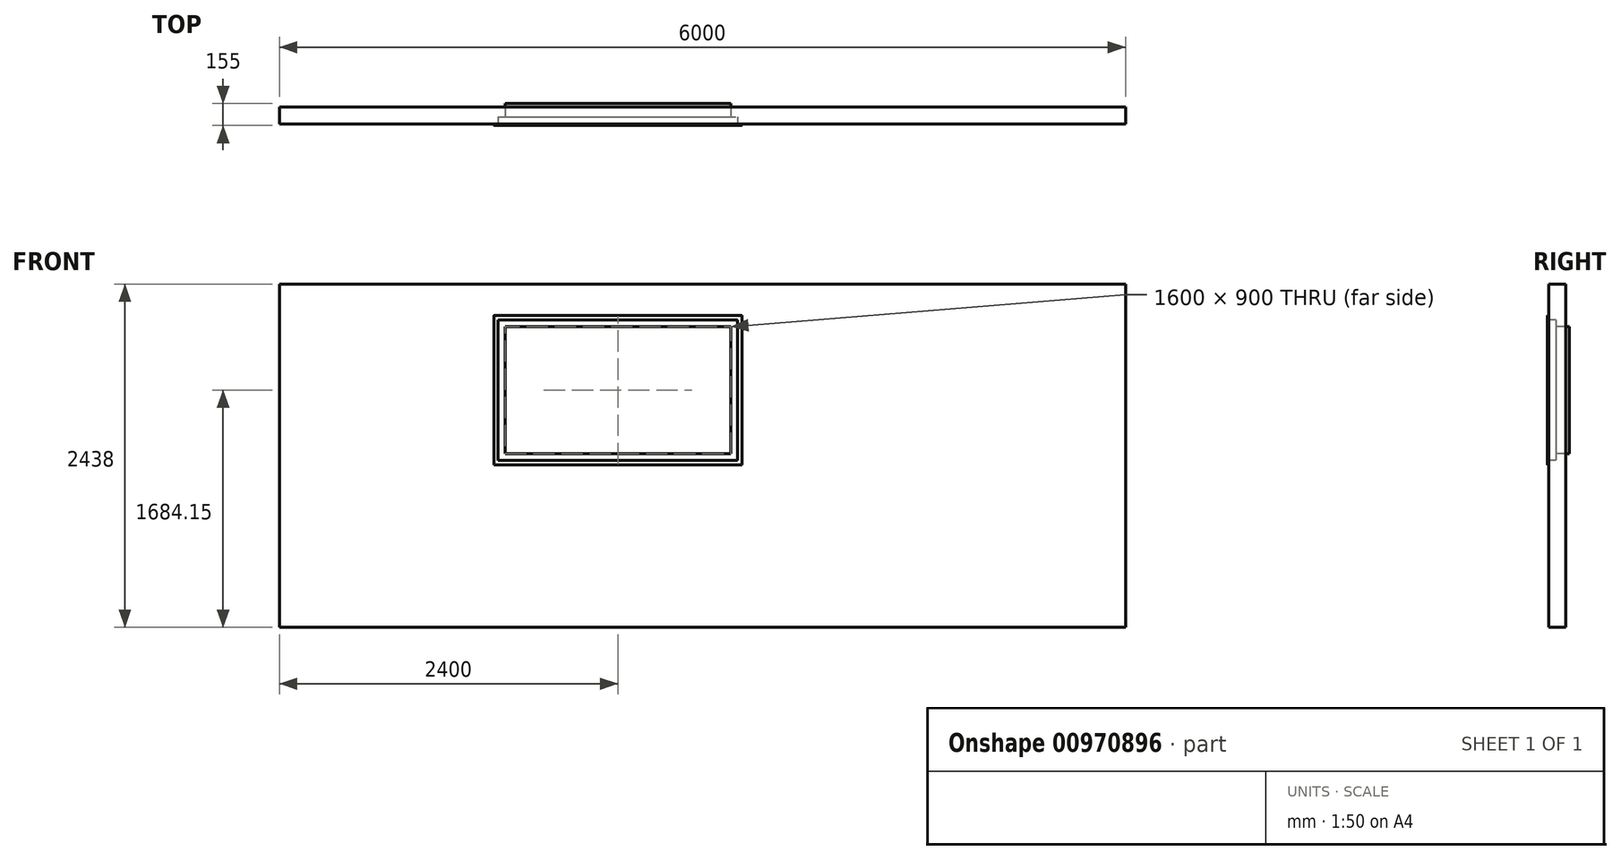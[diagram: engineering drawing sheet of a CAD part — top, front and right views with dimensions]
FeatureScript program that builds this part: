
annotation { "Feature Type Name" : "Feature", "Feature Type Description" : "" }
export const myFeature = defineFeature(function(context is Context, id is Id, definition is map)
    precondition{}
    {
        {
            var Q0;
            Q0=qCreatedBy(makeId("Front.planeOp"),FACE);
            var sketch = newSketch(context, id + "F0", { "sketchPlane" : qUnion([Q0])});
            skLineSegment(sketch, "E0.bottom", {"start": v(-2781.5, -1157.02) * mm, "end": v(3218.5, -1157.02) * mm});
            skLineSegment(sketch, "E0.top", {"start": v(-2781.5, 1280.98) * mm, "end": v(3218.5, 1280.98) * mm});
            skLineSegment(sketch, "E0.left", {"start": v(-2781.5, -1157.02) * mm, "end": v(-2781.5, 1280.98) * mm});
            skLineSegment(sketch, "E0.right", {"start": v(3218.5, -1157.02) * mm, "end": v(3218.5, 1280.98) * mm});
            skSolve(sketch);
        }
        {
            var Q0;
            Q0 = qSketchRegion(id + "F0", true);
            extrude(context, id + "F1", {"entities" : qUnion([Q0]), "depth" : 120 * mm, "offsetDistance" : 25 * mm});
        }
        {
            var Q0;
            Q0=makeQuery(id+"F1.opExtrude","CAP_FACE",FACE,{"disambiguationData":[OSD([sQuery(id+"F0.wireOp",EDGE,"E0.bottom"),sQuery(id+"F0.wireOp",EDGE,"E0.top"),sQuery(id+"F0.wireOp",EDGE,"E0.left"),sQuery(id+"F0.wireOp",EDGE,"E0.right")])],"isStart":false});
            var sketch = newSketch(context, id + "F2", { "sketchPlane" : qUnion([Q0])});
            skLineSegment(sketch, "E1.bottom", {"start": v(-1181.5, 977.13) * mm, "end": v(418.5, 977.13) * mm});
            skLineSegment(sketch, "E1.top", {"start": v(-1181.5, 77.13) * mm, "end": v(418.5, 77.13) * mm});
            skLineSegment(sketch, "E1.left", {"start": v(-1181.5, 977.13) * mm, "end": v(-1181.5, 77.13) * mm});
            skLineSegment(sketch, "E1.right", {"start": v(418.5, 977.13) * mm, "end": v(418.5, 77.13) * mm});
            skSolve(sketch);
        }
        {
            var Q0;
            Q0=makeQuery(id+"F2.imprint","IMPRINT",FACE,{"disambiguationData":[TD([[makeQuery(id+"F2.imprint","IMPRINT",EDGE,{"derivedFrom":sQuery(id+"F2.wireOp",EDGE,"E1.bottom")}),-1.0]])]});
            extrude(context, id + "F3", {"entities" : qUnion([Q0]), "operationType" : NewBodyOperationType.REMOVE, "endBound" : BoundingType.THROUGH_ALL, "oppositeDirection" : true, "depth" : 25 * mm, "offsetDistance" : 25 * mm});
        }
        {
            var Q0;
            Q0=makeQuery(id+"F1.opExtrude","CAP_FACE",FACE,{"disambiguationData":[OSD([sQuery(id+"F0.wireOp",EDGE,"E0.bottom"),sQuery(id+"F0.wireOp",EDGE,"E0.top"),sQuery(id+"F0.wireOp",EDGE,"E0.left"),sQuery(id+"F0.wireOp",EDGE,"E0.right")])],"isStart":false});
            var sketch = newSketch(context, id + "F4", { "sketchPlane" : qUnion([Q0])});
            skLineSegment(sketch, "E2.bottom", {"start": v(-1181.5, 977.13) * mm, "end": v(418.5, 977.13) * mm});
            skLineSegment(sketch, "E2.top", {"start": v(-1181.5, 77.13) * mm, "end": v(418.5, 77.13) * mm});
            skLineSegment(sketch, "E2.left", {"start": v(-1181.5, 977.13) * mm, "end": v(-1181.5, 77.13) * mm});
            skLineSegment(sketch, "E2.right", {"start": v(418.5, 977.13) * mm, "end": v(418.5, 77.13) * mm});
            skLineSegment(sketch, "E3.bottom", {"start": v(-1231.5, 1027.13) * mm, "end": v(468.5, 1027.13) * mm});
            skLineSegment(sketch, "E3.top", {"start": v(-1231.5, 27.13) * mm, "end": v(468.5, 27.13) * mm});
            skLineSegment(sketch, "E3.left", {"start": v(-1231.5, 1027.13) * mm, "end": v(-1231.5, 27.13) * mm});
            skLineSegment(sketch, "E3.right", {"start": v(468.5, 1027.13) * mm, "end": v(468.5, 27.13) * mm});
            skSolve(sketch);
        }
        {
            var Q0;
            Q0=makeQuery(id+"F4.imprint","IMPRINT",FACE,{"disambiguationData":[TD([[makeQuery(id+"F4.imprint","IMPRINT",EDGE,{"derivedFrom":sQuery(id+"F4.wireOp",EDGE,"E2.bottom")}),1.0]])]});
            extrude(context, id + "F5", {"entities" : qUnion([Q0]), "operationType" : NewBodyOperationType.REMOVE, "oppositeDirection" : true, "depth" : 50 * mm, "offsetDistance" : 25 * mm});
        }
        {
            var Q0;
            Q0=makeQuery(id+"F1.opExtrude","CAP_FACE",FACE,{"disambiguationData":[OSD([sQuery(id+"F0.wireOp",EDGE,"E0.bottom"),sQuery(id+"F0.wireOp",EDGE,"E0.top"),sQuery(id+"F0.wireOp",EDGE,"E0.left"),sQuery(id+"F0.wireOp",EDGE,"E0.right")])],"isStart":false});
            var sketch = newSketch(context, id + "F6", { "sketchPlane" : qUnion([Q0])});
            skLineSegment(sketch, "E4.bottom", {"start": v(-1261.5, 1057.13) * mm, "end": v(498.5, 1057.13) * mm});
            skLineSegment(sketch, "E4.top", {"start": v(-1261.5, -2.87) * mm, "end": v(498.5, -2.87) * mm});
            skLineSegment(sketch, "E4.left", {"start": v(-1261.5, 1057.13) * mm, "end": v(-1261.5, -2.87) * mm});
            skLineSegment(sketch, "E4.right", {"start": v(498.5, 1057.13) * mm, "end": v(498.5, -2.87) * mm});
            skLineSegment(sketch, "E5.bottom", {"start": v(-1231.5, 1027.13) * mm, "end": v(468.5, 1027.13) * mm});
            skLineSegment(sketch, "E5.top", {"start": v(-1231.5, 27.13) * mm, "end": v(468.5, 27.13) * mm});
            skLineSegment(sketch, "E5.left", {"start": v(-1231.5, 1027.13) * mm, "end": v(-1231.5, 27.13) * mm});
            skLineSegment(sketch, "E5.right", {"start": v(468.5, 1027.13) * mm, "end": v(468.5, 27.13) * mm});
            skSolve(sketch);
        }
        {
            var Q0;
            Q0=makeQuery(id+"F6.imprint","IMPRINT",FACE,{"disambiguationData":[TD([[makeQuery(id+"F6.imprint","IMPRINT",EDGE,{"derivedFrom":sQuery(id+"F6.wireOp",EDGE,"E4.bottom")}),-1.0]])]});
            extrude(context, id + "F7", {"entities" : qUnion([Q0]), "operationType" : NewBodyOperationType.ADD, "depth" : 10 * mm, "offsetDistance" : 25 * mm});
        }
        {
            var Q0;
            Q0=makeQuery(id+"F7.opExtrude","CAP_EDGE",EDGE,{"disambiguationData":[OSD([sQuery(id+"F6.wireOp",EDGE,"E4.bottom")])],"isStart":false});
            var Q1;
            Q1=makeQuery(id+"F7.opExtrude","CAP_EDGE",EDGE,{"disambiguationData":[OSD([sQuery(id+"F6.wireOp",EDGE,"E4.right")])],"isStart":false});
            var Q2;
            Q2=makeQuery(id+"F7.opExtrude","CAP_EDGE",EDGE,{"disambiguationData":[OSD([sQuery(id+"F6.wireOp",EDGE,"E4.top")])],"isStart":false});
            var Q3;
            Q3=makeQuery(id+"F7.opExtrude","CAP_EDGE",EDGE,{"disambiguationData":[OSD([sQuery(id+"F6.wireOp",EDGE,"E4.left")])],"isStart":false});
            fillet(context, id + "F8", {"entities" : qUnion([Q0, Q1, Q2, Q3]), "radius" : 5 * mm, "tangentPropagation" : true, "allowEdgeOverflow" : false});
        }
        {
            var Q0;
            Q0=makeQuery(id+"F1.opExtrude","CAP_FACE",FACE,{"disambiguationData":[OSD([sQuery(id+"F0.wireOp",EDGE,"E0.bottom"),sQuery(id+"F0.wireOp",EDGE,"E0.top"),sQuery(id+"F0.wireOp",EDGE,"E0.left"),sQuery(id+"F0.wireOp",EDGE,"E0.right")])],"isStart":true});
            var sketch = newSketch(context, id + "F9", { "sketchPlane" : qUnion([Q0])});
            skLineSegment(sketch, "E6.bottom", {"start": v(-418.5, 977.13) * mm, "end": v(1181.5, 977.13) * mm});
            skLineSegment(sketch, "E6.top", {"start": v(-418.5, 77.13) * mm, "end": v(1181.5, 77.13) * mm});
            skLineSegment(sketch, "E6.left", {"start": v(-418.5, 977.13) * mm, "end": v(-418.5, 77.13) * mm});
            skLineSegment(sketch, "E6.right", {"start": v(1181.5, 977.13) * mm, "end": v(1181.5, 77.13) * mm});
            skSolve(sketch);
        }
        {
            var Q0;
            Q0 = qSketchRegion(id + "F9", true);
            extrude(context, id + "F10", {"entities" : qUnion([Q0]), "depth" : 25 * mm, "offsetDistance" : 25 * mm});
        }
    });
